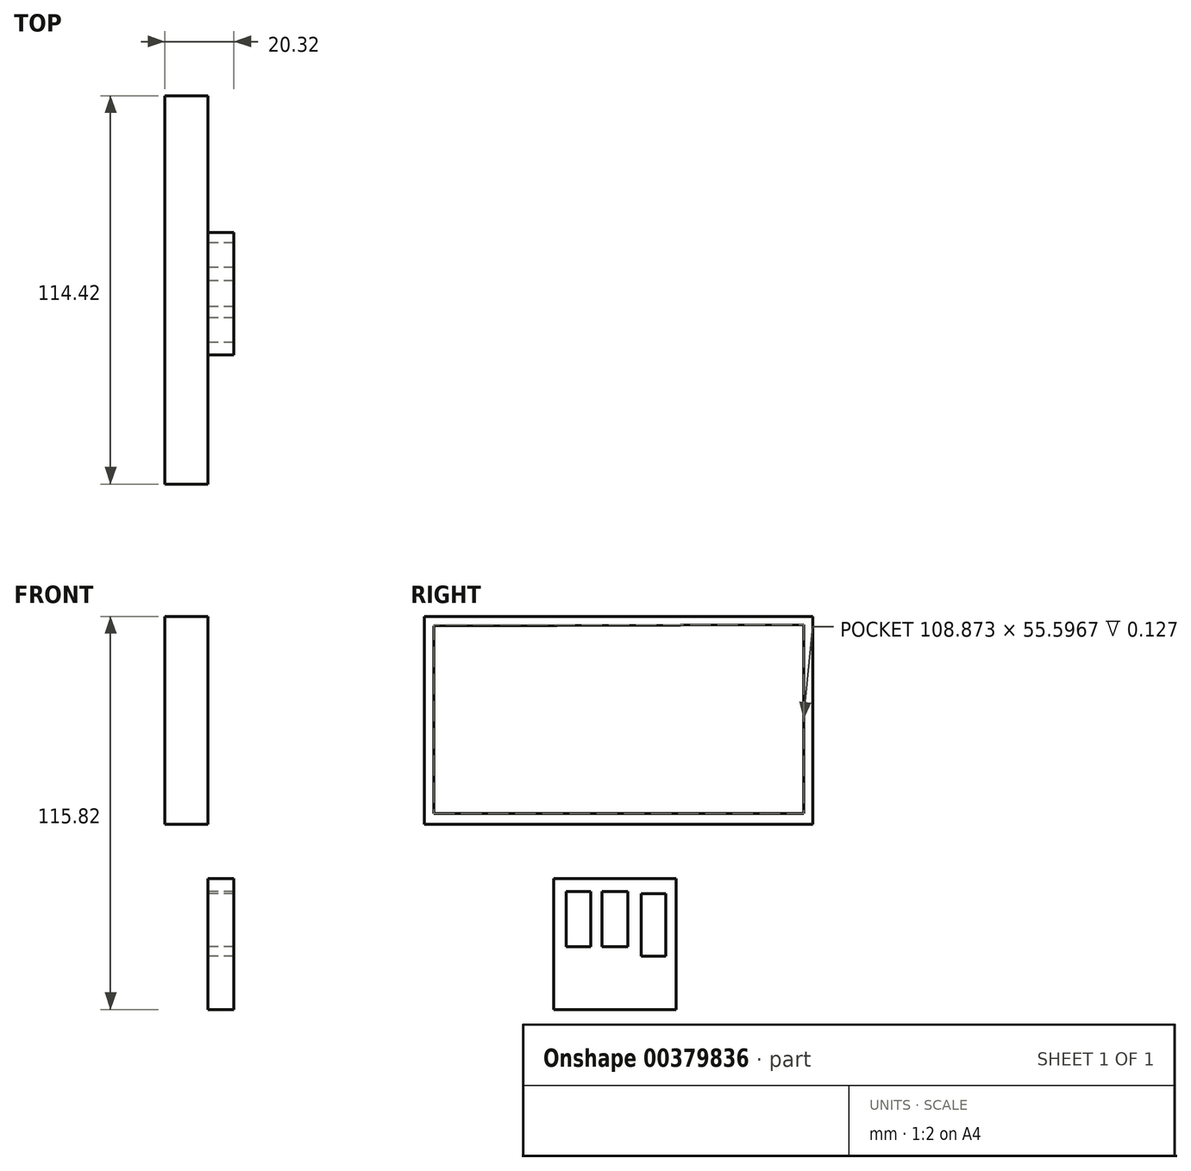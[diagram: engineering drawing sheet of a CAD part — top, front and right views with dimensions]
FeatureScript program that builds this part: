
annotation { "Feature Type Name" : "Feature", "Feature Type Description" : "" }
export const myFeature = defineFeature(function(context is Context, id is Id, definition is map)
    precondition{}
    {
        {
            var Q0;
            Q0=qCreatedBy(makeId("Right.planeOp"),FACE);
            var sketch = newSketch(context, id + "F0", { "sketchPlane" : qUnion([Q0])});
            skLineSegment(sketch, "E0.bottom", {"start": v(66.16, 63.5) * mm, "end": v(-66.16, 63.5) * mm});
            skLineSegment(sketch, "E0.top", {"start": v(66.16, -63.5) * mm, "end": v(-66.16, -63.5) * mm});
            skLineSegment(sketch, "E0.left", {"start": v(66.16, 63.5) * mm, "end": v(66.16, -63.5) * mm});
            skLineSegment(sketch, "E0.right", {"start": v(-66.16, 63.5) * mm, "end": v(-66.16, -63.5) * mm});
            skPoint(sketch, "E0.middle", {"position": v(0, 0) * mm});
            skLineSegment(sketch, "E1.bottom", {"start": v(58.05, 50.36) * mm, "end": v(-56.37, 50.36) * mm});
            skLineSegment(sketch, "E1.top", {"start": v(58.05, -10.91) * mm, "end": v(-56.37, -10.91) * mm});
            skLineSegment(sketch, "E1.left", {"start": v(58.05, 50.36) * mm, "end": v(58.05, -10.91) * mm});
            skLineSegment(sketch, "E1.right", {"start": v(-56.37, 50.36) * mm, "end": v(-56.37, -10.91) * mm});
            skLineSegment(sketch, "E2.bottom", {"start": v(20.84, -56.23) * mm, "end": v(-21.4, -56.23) * mm});
            skLineSegment(sketch, "E2.top", {"start": v(20.84, -15.95) * mm, "end": v(-21.4, -15.95) * mm});
            skLineSegment(sketch, "E2.left", {"start": v(20.84, -56.23) * mm, "end": v(20.84, -15.95) * mm});
            skLineSegment(sketch, "E2.right", {"start": v(-21.4, -56.23) * mm, "end": v(-21.4, -15.95) * mm});
            skLineSegment(sketch, "E3.bottom", {"start": v(16.37, -24.9) * mm, "end": v(10.21, -24.9) * mm});
            skLineSegment(sketch, "E3.top", {"start": v(16.37, -37.2) * mm, "end": v(10.21, -37.2) * mm});
            skLineSegment(sketch, "E3.left", {"start": v(16.37, -24.9) * mm, "end": v(16.37, -37.2) * mm});
            skLineSegment(sketch, "E3.right", {"start": v(10.21, -24.9) * mm, "end": v(10.21, -37.2) * mm});
            skLineSegment(sketch, "E4.bottom", {"start": v(3.22, -24.62) * mm, "end": v(-4.06, -24.62) * mm});
            skLineSegment(sketch, "E4.top", {"start": v(3.22, -37.2) * mm, "end": v(-4.06, -37.2) * mm});
            skLineSegment(sketch, "E4.left", {"start": v(3.22, -24.62) * mm, "end": v(3.22, -37.2) * mm});
            skLineSegment(sketch, "E4.right", {"start": v(-4.06, -24.62) * mm, "end": v(-4.06, -37.2) * mm});
            skLineSegment(sketch, "E5.bottom", {"start": v(-10.5, -24.34) * mm, "end": v(-17.48, -24.34) * mm});
            skLineSegment(sketch, "E5.top", {"start": v(-10.5, -37.2) * mm, "end": v(-17.48, -37.2) * mm});
            skLineSegment(sketch, "E5.left", {"start": v(-10.5, -24.34) * mm, "end": v(-10.5, -37.2) * mm});
            skLineSegment(sketch, "E5.right", {"start": v(-17.48, -24.34) * mm, "end": v(-17.48, -37.2) * mm});
            skPoint(sketch, "E6.oppositeSnap0", {"position": v(13.29, -37.2) * mm});
            skLineSegment(sketch, "E6.bottom", {"start": v(13.29, -37.2) * mm, "end": v(13.29, -37.2) * mm});
            skLineSegment(sketch, "E6.top", {"start": v(13.29, -56.23) * mm, "end": v(13.29, -56.23) * mm});
            skLineSegment(sketch, "E6.left", {"start": v(13.29, -37.2) * mm, "end": v(13.29, -56.23) * mm});
            skLineSegment(sketch, "E6.right", {"start": v(13.29, -37.2) * mm, "end": v(13.29, -56.23) * mm});
            skLineSegment(sketch, "E7.bottom", {"start": v(0, -37.2) * mm, "end": v(-0.28, -37.2) * mm});
            skLineSegment(sketch, "E7.top", {"start": v(0, -56.23) * mm, "end": v(-0.28, -56.23) * mm});
            skLineSegment(sketch, "E7.left", {"start": v(0, -37.2) * mm, "end": v(0, -56.23) * mm});
            skLineSegment(sketch, "E7.right", {"start": v(-0.28, -37.2) * mm, "end": v(-0.28, -56.23) * mm});
            skPoint(sketch, "E8.oppositeSnap0", {"position": v(-13.99, -37.2) * mm});
            skLineSegment(sketch, "E8.bottom", {"start": v(-13.99, -37.2) * mm, "end": v(-13.99, -37.2) * mm});
            skLineSegment(sketch, "E8.top", {"start": v(-13.99, -56.23) * mm, "end": v(-13.99, -56.23) * mm});
            skLineSegment(sketch, "E8.left", {"start": v(-13.99, -37.2) * mm, "end": v(-13.99, -56.23) * mm});
            skLineSegment(sketch, "E8.right", {"start": v(-13.99, -37.2) * mm, "end": v(-13.99, -56.23) * mm});
            skSolve(sketch);
        }
        {
            var Q0;
            Q0=makeQuery(id+"F0.imprint","IMPRINT",FACE,{"disambiguationData":[TD([[makeQuery(id+"F0.imprint","IMPRINT",EDGE,{"derivedFrom":sQuery(id+"F0.wireOp",EDGE,"E1.bottom")}),1.0]])]});
            extrude(context, id + "F1", {"entities" : qUnion([Q0]), "depth" : 25.4 * mm});
        }
        {
            var Q0;
            Q0=makeQuery(id+"F1.opExtrude","CAP_FACE",FACE,{"disambiguationData":[OSD([sQuery(id+"F0.wireOp",EDGE,"E1.bottom"),sQuery(id+"F0.wireOp",EDGE,"E1.top"),sQuery(id+"F0.wireOp",EDGE,"E1.left"),sQuery(id+"F0.wireOp",EDGE,"E1.right")])],"isStart":true});
            extrude(context, id + "F2", {"entities" : qUnion([Q0]), "operationType" : NewBodyOperationType.REMOVE, "oppositeDirection" : true, "depth" : 12.7 * mm});
        }
        {
            var Q0;
            Q0=qCreatedBy(makeId("Right.planeOp"),FACE);
            var sketch = newSketch(context, id + "F3", { "sketchPlane" : qUnion([Q0])});
            skLineSegment(sketch, "E9.bottom", {"start": v(17.76, -65.46) * mm, "end": v(-18.32, -65.46) * mm});
            skLineSegment(sketch, "E9.top", {"start": v(17.76, -26.86) * mm, "end": v(-18.32, -26.86) * mm});
            skLineSegment(sketch, "E9.left", {"start": v(17.76, -65.46) * mm, "end": v(17.76, -26.86) * mm});
            skLineSegment(sketch, "E9.right", {"start": v(-18.32, -65.46) * mm, "end": v(-18.32, -26.86) * mm});
            skLineSegment(sketch, "E10.bottom", {"start": v(14.69, -31.33) * mm, "end": v(7.41, -31.33) * mm});
            skLineSegment(sketch, "E10.top", {"start": v(14.69, -49.8) * mm, "end": v(7.41, -49.8) * mm});
            skLineSegment(sketch, "E10.left", {"start": v(14.69, -31.33) * mm, "end": v(14.69, -49.8) * mm});
            skLineSegment(sketch, "E10.right", {"start": v(7.41, -31.33) * mm, "end": v(7.41, -49.8) * mm});
            skLineSegment(sketch, "E11.bottom", {"start": v(3.5, -30.77) * mm, "end": v(-4.06, -30.77) * mm});
            skLineSegment(sketch, "E11.top", {"start": v(3.5, -47) * mm, "end": v(-4.06, -47) * mm});
            skLineSegment(sketch, "E11.left", {"start": v(3.5, -30.77) * mm, "end": v(3.5, -47) * mm});
            skLineSegment(sketch, "E11.right", {"start": v(-4.06, -30.77) * mm, "end": v(-4.06, -47) * mm});
            skLineSegment(sketch, "E12.bottom", {"start": v(-7.41, -30.77) * mm, "end": v(-14.69, -30.77) * mm});
            skLineSegment(sketch, "E12.top", {"start": v(-7.41, -47) * mm, "end": v(-14.69, -47) * mm});
            skLineSegment(sketch, "E12.left", {"start": v(-7.41, -30.77) * mm, "end": v(-7.41, -47) * mm});
            skLineSegment(sketch, "E12.right", {"start": v(-14.69, -30.77) * mm, "end": v(-14.69, -47) * mm});
            skPoint(sketch, "E13.oppositeSnap0", {"position": v(11.05, -49.8) * mm});
            skLineSegment(sketch, "E13.bottom", {"start": v(11.05, -49.8) * mm, "end": v(11.05, -49.8) * mm});
            skLineSegment(sketch, "E13.top", {"start": v(11.05, -59.87) * mm, "end": v(11.05, -59.87) * mm});
            skLineSegment(sketch, "E13.left", {"start": v(11.05, -49.8) * mm, "end": v(11.05, -59.87) * mm});
            skLineSegment(sketch, "E13.right", {"start": v(11.05, -49.8) * mm, "end": v(11.05, -59.87) * mm});
            skLineSegment(sketch, "E14.bottom", {"start": v(0, -47) * mm, "end": v(0, -47) * mm});
            skLineSegment(sketch, "E14.top", {"start": v(0, -59.87) * mm, "end": v(0, -59.87) * mm});
            skLineSegment(sketch, "E14.left", {"start": v(0, -47) * mm, "end": v(0, -59.87) * mm});
            skLineSegment(sketch, "E14.right", {"start": v(0, -47) * mm, "end": v(0, -59.87) * mm});
            skPoint(sketch, "E15.oppositeSnap0", {"position": v(-11.05, -47) * mm});
            skLineSegment(sketch, "E15.bottom", {"start": v(-11.05, -47) * mm, "end": v(-11.05, -47) * mm});
            skLineSegment(sketch, "E15.top", {"start": v(-11.05, -59.87) * mm, "end": v(-11.05, -59.87) * mm});
            skLineSegment(sketch, "E15.left", {"start": v(-11.05, -47) * mm, "end": v(-11.05, -59.87) * mm});
            skLineSegment(sketch, "E15.right", {"start": v(-11.05, -47) * mm, "end": v(-11.05, -59.87) * mm});
            skSolve(sketch);
        }
        {
            var Q0;
            Q0=makeQuery(id+"F3.imprint","IMPRINT",FACE,{"disambiguationData":[TD([[makeQuery(id+"F3.imprint","IMPRINT",EDGE,{"derivedFrom":sQuery(id+"F3.wireOp",EDGE,"E9.bottom")}),-1.0]])]});
            extrude(context, id + "F4", {"entities" : qUnion([Q0]), "depth" : 7.62 * mm});
        }
        {
            var Q0;
            Q0=makeQuery(id+"F4.opExtrude","CAP_FACE",FACE,{"disambiguationData":[OSD([sQuery(id+"F3.wireOp",EDGE,"E9.bottom"),sQuery(id+"F3.wireOp",EDGE,"E9.top"),sQuery(id+"F3.wireOp",EDGE,"E9.left"),sQuery(id+"F3.wireOp",EDGE,"E9.right"),sQuery(id+"F3.wireOp",EDGE,"E10.bottom"),sQuery(id+"F3.wireOp",EDGE,"E10.top"),sQuery(id+"F3.wireOp",EDGE,"E10.left"),sQuery(id+"F3.wireOp",EDGE,"E10.right"),sQuery(id+"F3.wireOp",EDGE,"E11.bottom"),sQuery(id+"F3.wireOp",EDGE,"E11.top"),sQuery(id+"F3.wireOp",EDGE,"E11.left"),sQuery(id+"F3.wireOp",EDGE,"E11.right"),sQuery(id+"F3.wireOp",EDGE,"E12.bottom"),sQuery(id+"F3.wireOp",EDGE,"E12.top"),sQuery(id+"F3.wireOp",EDGE,"E12.left"),sQuery(id+"F3.wireOp",EDGE,"E12.right")])],"isStart":false});
            extrude(context, id + "F5", {"entities" : qUnion([Q0]), "operationType" : NewBodyOperationType.ADD, "depth" : 25.4 * mm});
        }
        {
            var Q0;
            Q0=makeQuery(id+"F4.opExtrude","CAP_FACE",FACE,{"disambiguationData":[OSD([sQuery(id+"F3.wireOp",EDGE,"E9.bottom"),sQuery(id+"F3.wireOp",EDGE,"E9.top"),sQuery(id+"F3.wireOp",EDGE,"E9.left"),sQuery(id+"F3.wireOp",EDGE,"E9.right"),sQuery(id+"F3.wireOp",EDGE,"E10.bottom"),sQuery(id+"F3.wireOp",EDGE,"E10.top"),sQuery(id+"F3.wireOp",EDGE,"E10.left"),sQuery(id+"F3.wireOp",EDGE,"E10.right"),sQuery(id+"F3.wireOp",EDGE,"E11.bottom"),sQuery(id+"F3.wireOp",EDGE,"E11.top"),sQuery(id+"F3.wireOp",EDGE,"E11.left"),sQuery(id+"F3.wireOp",EDGE,"E11.right"),sQuery(id+"F3.wireOp",EDGE,"E12.bottom"),sQuery(id+"F3.wireOp",EDGE,"E12.top"),sQuery(id+"F3.wireOp",EDGE,"E12.left"),sQuery(id+"F3.wireOp",EDGE,"E12.right")])],"isStart":true});
            extrude(context, id + "F6", {"entities" : qUnion([Q0]), "operationType" : NewBodyOperationType.REMOVE, "oppositeDirection" : true, "depth" : 25.4 * mm});
        }
        {
            var Q0;
            Q0=makeQuery(id+"F1.opExtrude","CAP_FACE",FACE,{"disambiguationData":[OSD([sQuery(id+"F0.wireOp",EDGE,"E1.bottom"),sQuery(id+"F0.wireOp",EDGE,"E1.top"),sQuery(id+"F0.wireOp",EDGE,"E1.left"),sQuery(id+"F0.wireOp",EDGE,"E1.right")])],"isStart":false});
            var sketch = newSketch(context, id + "F7", { "sketchPlane" : qUnion([Q0])});
            skLineSegment(sketch, "E16", {"start": v(-53.57, 47.56) * mm, "end": v(-53.57, -7.71) * mm});
            skLineSegment(sketch, "E17", {"start": v(-53.57, -7.71) * mm, "end": v(55.3, -7.71) * mm});
            skLineSegment(sketch, "E18", {"start": v(55.3, -7.71) * mm, "end": v(55.3, 47.88) * mm});
            skLineSegment(sketch, "E19", {"start": v(-53.57, 47.56) * mm, "end": v(55.3, 47.88) * mm});
            skSolve(sketch);
        }
        {
            var Q0;
            Q0=makeQuery(id+"F7.imprint","IMPRINT",FACE,{"disambiguationData":[TD([[makeQuery(id+"F7.imprint","IMPRINT",EDGE,{"derivedFrom":sQuery(id+"F7.wireOp",EDGE,"E16")}),1.0]])]});
            extrude(context, id + "F8", {"entities" : qUnion([Q0]), "operationType" : NewBodyOperationType.REMOVE, "oppositeDirection" : true, "depth" : 0.13 * mm});
        }
    });
